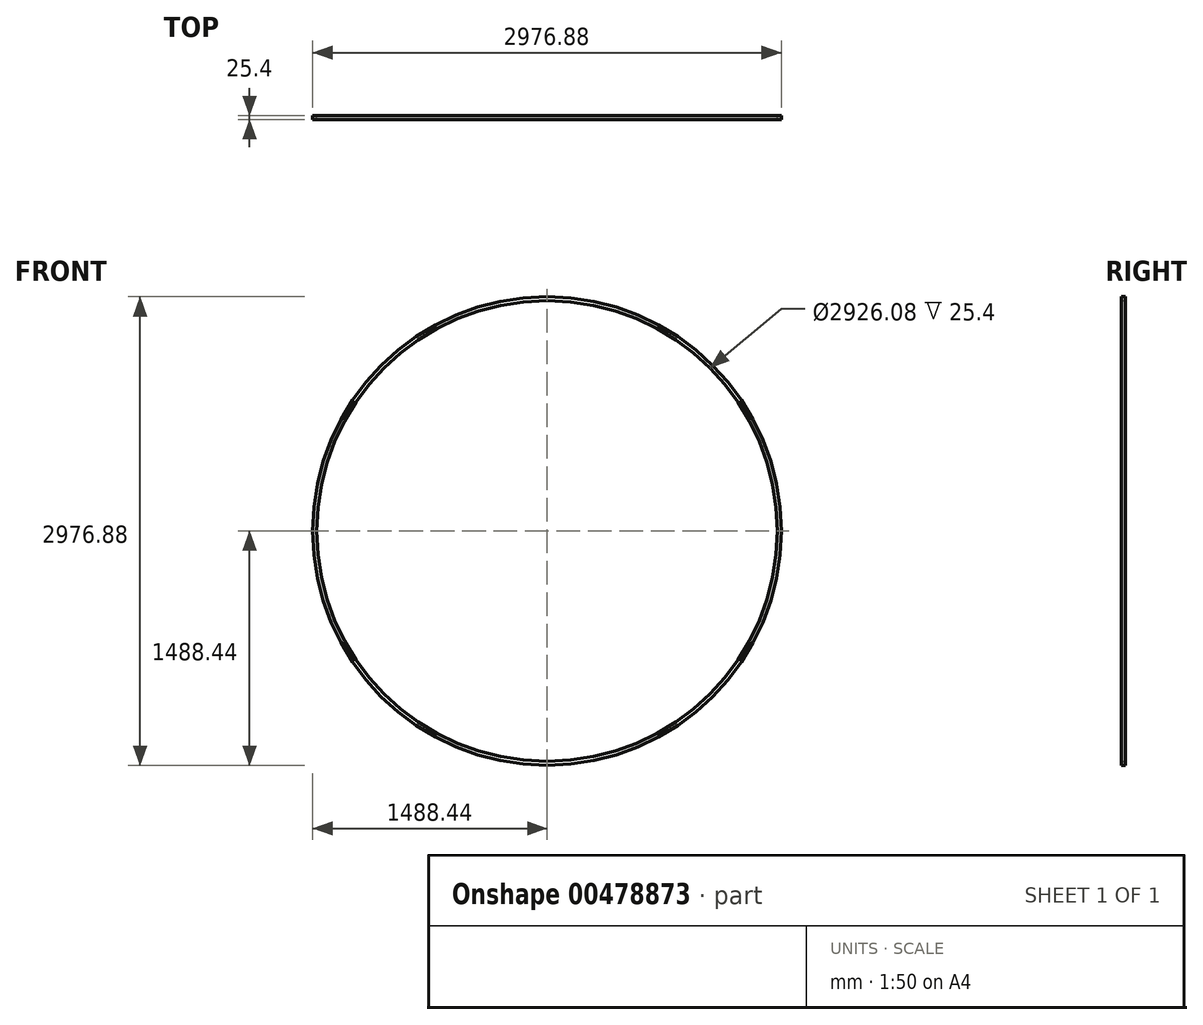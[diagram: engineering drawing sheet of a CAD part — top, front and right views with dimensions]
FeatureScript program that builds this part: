
annotation { "Feature Type Name" : "Feature", "Feature Type Description" : "" }
export const myFeature = defineFeature(function(context is Context, id is Id, definition is map)
    precondition{}
    {
        {
            var Q0;
            Q0=qCreatedBy(makeId("Front.planeOp"),FACE);
            var sketch = newSketch(context, id + "F0", { "sketchPlane" : qUnion([Q0])});
            skCircle(sketch, "E0", {"center": v(0, 0) * mm, "radius": 1488.44 * mm});
            skCircle(sketch, "E1", {"center": v(0, 0) * mm, "radius": 1463.04 * mm});
            skSolve(sketch);
        }
        {
            var Q0;
            Q0=makeQuery(id+"F0.imprint","IMPRINT",FACE,{"disambiguationData":[TD([[makeQuery(id+"F0.imprint","IMPRINT",EDGE,{"derivedFrom":sQuery(id+"F0.wireOp",EDGE,"E0")}),1.0]])]});
            extrude(context, id + "F1", {"entities" : qUnion([Q0]), "depth" : 25.4 * mm});
        }
    });
